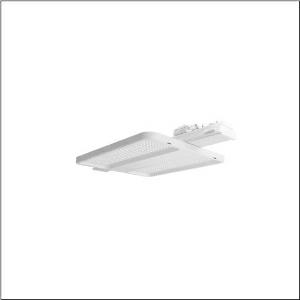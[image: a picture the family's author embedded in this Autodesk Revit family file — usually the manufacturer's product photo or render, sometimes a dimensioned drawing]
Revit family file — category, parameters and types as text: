
# Revit family: highbay_11_fur_licross_tragschiene_midi_51hn12da4fla
name_source: partatom
category: Lighting Fixtures
units: mm (PartAtom-declared; Revit-internal decimal feet)

## family parameters
Cut with Voids When Loaded = No
Host = Face
Light Source = No
Part Type = Normal
Room Calculation Point = No
Round Connector Dimension = Use Diameter
Shared = No

## types (1)
- --- (1 x LED, 15000 lm, 73.2 W, 4000K)
    Apparent Load = 73 VA
    CIE Flux Codes = 87 98 100 100 100
    Color Rendering = 80
    Color Temperature = 4000K
    Default Elevation = 1800 mm
    Description = high bay luminaire Highbay 11 for Licross trunking rail midi; direct symmetric wide distribution, light control with lens of PMMA; UGR ≤ 22 (X = 4H | Y = 8H | S = 0.25H | reflection values 70/50/20); luminous flux: 15.000lm; light colour: 840, colour temperature: 4000K, MacAdam ≤ 2 SDCM (initial), colour rendering: CRI > 80; luminous efficacy: 204,9lm/W; rated service life: 100.000h (L95) at AT= 25°C; control: DALI 2; luminaire connection: plug, 5-pole, with phase selectionmains connection: 230..240V, AC 50/60Hz; connected load: 73,2W; protection rating (complete): IP64; insulation class (complete): insulation class I (protective earthing); protection symbol: D; impact resistance: IK06; certification: CE, ENEC, VDE, UKCA; internal wiring halogen-free; luminaire LABS conformity tested according to VDMA 24364:2018-05; Suitable for use in the food industry according to the specifications of IFS-Food, HACCP and/or BRC; housing frame of high-performance plastic PA6, matt traffic white (RAL 9016); cover of PMMA; fixing on rail side of steel, galvanised, white; blank cover of PC/ABS, traffic white (RAL 9016); dimension (LxWxH): 750 x 442 x 71mm; permissible operating ambient temperature: -40..+55°C (reducing of maximum allowable ambient temperature of 5°C with ceiling mounting); packaging unit: 1 piece
    Height = 72 mm  [stored 0.23622 ft]
    Lamp = 1 x LED
    Lamp Light Flux = 15000 lm
    Lamp Power = 73.2 W
    Lamp count = 1
    Length = 474 mm
    Luminous efficacy = 205 lm/W
    Manufacturer = Siteco
    ModVariant = No
    Model = 51HN12DA4FLA
    Mounting Place = Ceiling
    Mounting Type = Pendant
    Number of Poles = 1
    OnlyDefault = Yes
    Power Factor = 1
    Product Name = Highbay 11 für Licross Tragschiene midi
    Product group = high bay luminaire
    ProductGroupID = 902
    Protection Class = Protection class I
    Protection Degree = IP 64
    RLX_Detail_Level = 1
    RLX_Emergency_Light_Flux = 0 lm
    RLX_Emergency_Type = 0
    RLX_Emergency_Type_DB = No
    RlxData = <blob elided: 16965 chars, md5=a0e14653>
    Socket = socket
    Standby Power = 0 W
    System Light Flux = 15000 lm
    System Power = 73 W
    Type Comments = factory setting: luminous flux: 100 % | dim-lin: 254 | 339 mA
    Type Image = l_1363258.jpg
    URL = http://relux.com
    VarID = @adj_027245
    Voltage = 0 V
    Weight = 0.00 kg
    Width = 442 mm

note: [stored X ft] marks values corroborated as IEEE doubles in the binary element streams (Revit-internal decimal feet)

## geometry (parser evidence)
native form markers: Blend x4, Sweep x12
no freeform markers — native parametric forms only
